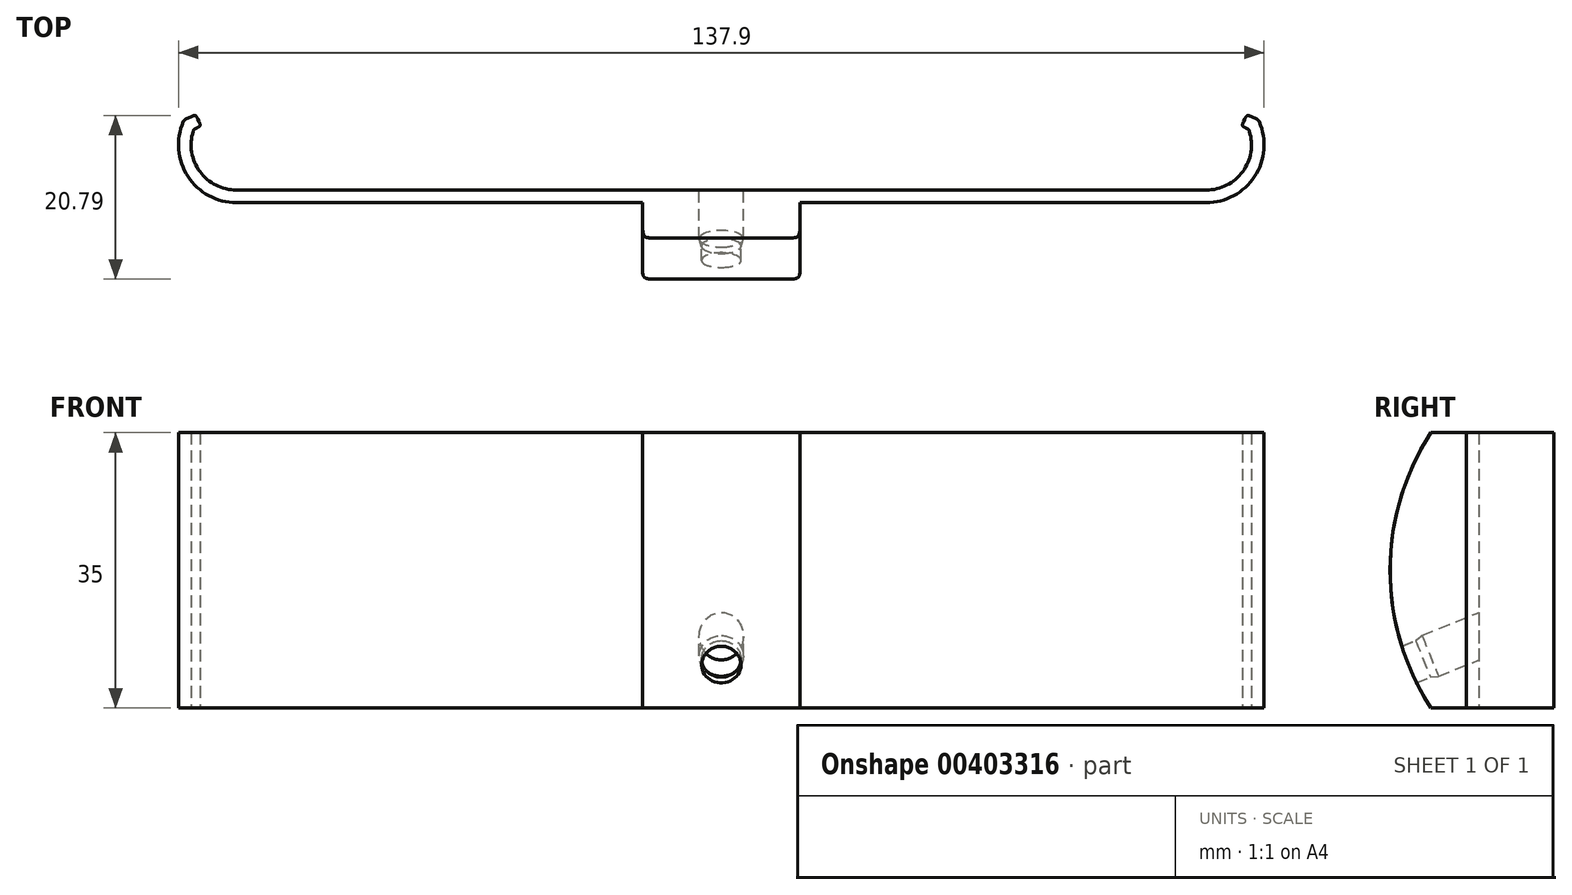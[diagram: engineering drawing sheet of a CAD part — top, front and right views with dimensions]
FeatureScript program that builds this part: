
annotation { "Feature Type Name" : "Feature", "Feature Type Description" : "" }
export const myFeature = defineFeature(function(context is Context, id is Id, definition is map)
    precondition{}
    {
        {
            var Q0;
            Q0=qCreatedBy(makeId("Top.planeOp"),FACE);
            var sketch = newSketch(context, id + "F0", { "sketchPlane" : qUnion([Q0])});
            skLineSegment(sketch, "E0", {"start": v(0, 0) * mm, "end": v(61.6, 0) * mm});
            skLineSegment(sketch, "E1", {"start": v(67, 7.72) * mm, "end": v(66.1, 8.14) * mm});
            skArc(sketch, "E2", {"start": v(61.6, 0) * mm, "mid": v(66.3, 2.45) * mm, "end": v(67, 7.72) * mm});
            skLineSegment(sketch, "E3", {"start": v(61.6, 5.75) * mm, "end": v(67, 7.72) * mm, "construction": true});
            skLineSegment(sketch, "E4", {"start": v(67, 7.72) * mm, "end": v(65.65, 11.43) * mm, "construction": true});
            skLineSegment(sketch, "E5", {"start": v(0, 0) * mm, "end": v(0, -1.6) * mm});
            skLineSegment(sketch, "E6", {"start": v(0, -1.6) * mm, "end": v(61.6, -1.6) * mm});
            skArc(sketch, "E7", {"start": v(61.6, -1.6) * mm, "mid": v(67.81, 1.82) * mm, "end": v(68.23, 8.9) * mm});
            skLineSegment(sketch, "E8", {"start": v(68.23, 8.9) * mm, "end": v(66.77, 9.59) * mm});
            skLineSegment(sketch, "E9", {"start": v(66.77, 9.59) * mm, "end": v(66.1, 8.14) * mm});
            skSolve(sketch);
        }
        {
            var Q0;
            Q0=qSketchRegion(id+"F0",true);
            extrude(context, id + "F1", {"entities" : qUnion([Q0]), "endBound" : BoundingType.SYMMETRIC, "depth" : 35 * mm});
        }
        {
            var Q0;
            Q0=makeQuery(id+"F1.opExtrude","SWEPT_EDGE",EDGE,{"disambiguationData":[OSD([sQuery(id+"F0.wireOp",EDGE,"E1"),sQuery(id+"F0.wireOp",EDGE,"E2")])]});
            var Q1;
            Q1=makeQuery(id+"F1.opExtrude","SWEPT_EDGE",EDGE,{"disambiguationData":[OSD([sQuery(id+"F0.wireOp",EDGE,"E1"),sQuery(id+"F0.wireOp",EDGE,"E9")])]});
            var Q2;
            Q2=makeQuery(id+"F1.opExtrude","SWEPT_EDGE",EDGE,{"disambiguationData":[OSD([sQuery(id+"F0.wireOp",EDGE,"E8"),sQuery(id+"F0.wireOp",EDGE,"E9")])]});
            var Q3;
            Q3=makeQuery(id+"F1.opExtrude","SWEPT_EDGE",EDGE,{"disambiguationData":[OSD([sQuery(id+"F0.wireOp",EDGE,"E7"),sQuery(id+"F0.wireOp",EDGE,"E8")])]});
            fillet(context, id + "F2", {"entities" : qUnion([Q0, Q1, Q2, Q3]), "radius" : .6 * mm, "tangentPropagation" : true, "rho" : .7, "crossSection" : FilletCrossSection.CONIC, "allowEdgeOverflow" : false});
        }
        {
            var Q0;
            Q0=makeQuery(id+"F1.opExtrude","SWEPT_FACE",FACE,{"disambiguationData":[OSD([sQuery(id+"F0.wireOp",EDGE,"E5")])]});
            var sketch = newSketch(context, id + "F3", { "sketchPlane" : qUnion([Q0])});
            skLineSegment(sketch, "E10", {"start": v(1.6, -17.5) * mm, "end": v(1.6, 17.5) * mm});
            skLineSegment(sketch, "E11", {"start": v(1.6, 17.5) * mm, "end": v(6.1, 17.5) * mm});
            skLineSegment(sketch, "E12", {"start": v(6.1, -17.5) * mm, "end": v(1.6, -17.5) * mm});
            skArc(sketch, "E13", {"start": v(6.1, -17.5) * mm, "mid": v(11.3, 0) * mm, "end": v(6.1, 17.5) * mm});
            skSolve(sketch);
        }
        {
            var Q0;
            Q0 = qSketchRegion(id + "F3", true);
            extrude(context, id + "F4", {"entities" : qUnion([Q0]), "operationType" : NewBodyOperationType.ADD, "oppositeDirection" : true, "depth" : 10 * mm});
        }
        {
            var Q0;
            Q0=makeQuery(id+"F4.boolean.opBoolean","MERGE",FACE,{"derivedFrom":[makeQuery(id+"F1.opExtrude","SWEPT_FACE",FACE,{"disambiguationData":[OSD([sQuery(id+"F0.wireOp",EDGE,"E5")])]}),makeQuery(id+"F4.opExtrude","CAP_FACE",FACE,{"disambiguationData":[OSD([sQuery(id+"F3.wireOp",EDGE,"E10"),sQuery(id+"F3.wireOp",EDGE,"E11"),sQuery(id+"F3.wireOp",EDGE,"E12"),sQuery(id+"F3.wireOp",EDGE,"E13")])],"isStart":true})]});
            var sketch = newSketch(context, id + "F5", { "sketchPlane" : qUnion([Q0])});
            skLineSegment(sketch, "E14", {"start": v(8.04, -14.32) * mm, "end": v(8.97, -12) * mm, "construction": true});
            skLineSegment(sketch, "E15", {"start": v(8.97, -12) * mm, "end": v(2.95, -9.56) * mm});
            skLineSegment(sketch, "E16", {"start": v(2.95, -9.56) * mm, "end": v(1.9, -12.16) * mm, "construction": true});
            skLineSegment(sketch, "E17", {"start": v(0, 0) * mm, "end": v(8.97, 0) * mm, "construction": true});
            skPoint(sketch, "E17.endSnap0", {"position": v(11.3, 0) * mm});
            skLineSegment(sketch, "E18", {"start": v(8.97, 0) * mm, "end": v(8.97, -12) * mm, "construction": true});
            skLineSegment(sketch, "E19", {"start": v(8.04, -14.32) * mm, "end": v(6.18, -13.57) * mm});
            skLineSegment(sketch, "E20", {"start": v(6.18, -13.57) * mm, "end": v(5.14, -13.47) * mm});
            skLineSegment(sketch, "E21", {"start": v(5.14, -13.47) * mm, "end": v(1.9, -12.16) * mm});
            skLineSegment(sketch, "E22", {"start": v(2.95, -9.56) * mm, "end": v(-2.61, -7.31) * mm});
            skLineSegment(sketch, "E23", {"start": v(-2.61, -7.31) * mm, "end": v(-3.66, -9.9) * mm});
            skLineSegment(sketch, "E24", {"start": v(-3.66, -9.9) * mm, "end": v(1.9, -12.16) * mm});
            skLineSegment(sketch, "E25", {"start": v(8.97, -12) * mm, "end": v(14.54, -14.25) * mm});
            skLineSegment(sketch, "E26", {"start": v(14.54, -14.25) * mm, "end": v(13.6, -16.57) * mm});
            skLineSegment(sketch, "E27", {"start": v(13.6, -16.57) * mm, "end": v(8.04, -14.32) * mm});
            skSolve(sketch);
        }
        {
            var Q0;
            Q0 = qSketchRegion(id + "F5", true);
            var Q1;
            Q1=sQuery(id+"F5.wireOp",EDGE,"E15");
            revolve(context, id + "F6", {"operationType" : NewBodyOperationType.REMOVE, "entities" : qUnion([Q0]), "axis" : qUnion([Q1]), "revolveType" : RevolveType.FULL, "oppositeDirection" : true});
        }
        {
            var Q0;
            Q0=makeQuery(id+"F1.opExtrude","SWEPT_BODY",BODY,{"disambiguationData":[OSD([sQuery(id+"F0.wireOp",EDGE,"E0"),sQuery(id+"F0.wireOp",EDGE,"E1"),sQuery(id+"F0.wireOp",EDGE,"E2"),sQuery(id+"F0.wireOp",EDGE,"E5"),sQuery(id+"F0.wireOp",EDGE,"E6"),sQuery(id+"F0.wireOp",EDGE,"E7"),sQuery(id+"F0.wireOp",EDGE,"E8"),sQuery(id+"F0.wireOp",EDGE,"E9")])]});
            var Q1;
            Q1=qCreatedBy(makeId("Right.planeOp"),FACE);
            mirror(context, id + "F7", {"operationType" : NewBodyOperationType.ADD, "entities" : qUnion([Q0]), "mirrorPlane" : qUnion([Q1])});
        }
        {
            var Q0;
            Q0=makeQuery(id+"F4.opExtrude","CAP_EDGE",EDGE,{"disambiguationData":[OSD([sQuery(id+"F3.wireOp",EDGE,"E10")])],"isStart":false});
            var Q1;
            Q1=makeQuery(id+"F4.opExtrude","CAP_EDGE",EDGE,{"disambiguationData":[OSD([sQuery(id+"F3.wireOp",EDGE,"E13")])],"isStart":false});
            var Q2;
            Q2=makeQuery(id+"F7.opPattern","COPY",EDGE,{"derivedFrom":makeQuery(id+"F4.opExtrude","CAP_EDGE",EDGE,{"disambiguationData":[OSD([sQuery(id+"F3.wireOp",EDGE,"E13")])],"isStart":false}),"instanceName":"1"});
            var Q3;
            Q3=makeQuery(id+"F7.opPattern","COPY",EDGE,{"derivedFrom":makeQuery(id+"F4.opExtrude","CAP_EDGE",EDGE,{"disambiguationData":[OSD([sQuery(id+"F3.wireOp",EDGE,"E10")])],"isStart":false}),"instanceName":"1"});
            fillet(context, id + "F8", {"entities" : qUnion([Q0, Q1, Q2, Q3]), "radius" : 1.5 * mm, "tangentPropagation" : true, "rho" : .7, "crossSection" : FilletCrossSection.CONIC, "allowEdgeOverflow" : false});
        }
    });
